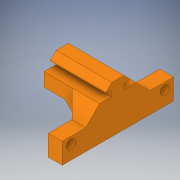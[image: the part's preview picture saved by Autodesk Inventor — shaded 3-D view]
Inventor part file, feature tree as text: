
AUTODESK INVENTOR PART (.ipt)
format: ipt  version: 2019 (Build 230136000, 136)  size: 202,752 bytes
history: native  units: in
note: dims shown in document units (in); Inventor stores cm internally (conversion verified against a paired STEP export)
features: sketch x5, extrude x4, chamfer x3, fillet x1, thicken_offset x1, hole x1, projected_geometry x1
ambient origin geometry x8: Origin, YZ Plane, XZ Plane, XY Plane, X Axis, Y Axis, Z Axis, Center Point
bodies: Body1 (feature_tree)
feature tree (16):
  extrude  "Extrusion2"  Depth=0.1in
  fillet  "Fillet1"  Radius=0.121in
  thicken_offset  "Thicken1"
  extrude  "Extrusion3"  Depth=0.442in
  extrude  "Extrusion4"  TaperAngle=135.0deg  [1 undecoded]
  chamfer  "Chamfer1"  Distance=1.0in
  hole  "Hole1"  [1 undecoded]
  extrude  "Extrusion5"  Depth=0.375in
  chamfer  "Chamfer4"  Distance=0.15in
  chamfer  "Chamfer5"  Distance=0.625in
  sketch  "Sketch1"  dims[d1=0.655in d2=0.1in d9=0.121in]
  sketch  "Sketch2"  dims[d12=0.0in d15=0.442in d16=0.46in]
  sketch  "Sketch3"  dims[d20=135.0deg d21=135.0deg]
  projected_geometry  "Projected Loop1"
  sketch  "Sketch4"  dims[d26=0.115in]
  sketch  "Sketch5"  dims[d38=0.218in d41=1.0in d42=0.0in d43=0.01in d44=0.15in d45=0.15in d46=0.625in d47=0.25in d48=0.0in d49=2.0in d50=0.655in d51=0.6725in d52=0.375in d53=0.25in d54=0.0in d55=0.25in d56=0.125in d57=45.0deg d64=0.154in d66=0.154in d68=0.165in d69=0.75in d70=0.375in d71=0.25in d72=0.5635in d73=1.0in d74=0.8108in d75=0.154in d76=0.154in d77=0.23in d78=0.2125in d79=0.75in d80=0.0in d81=0.244in d82=0.125in d83=45.0deg d84=0.375in d85=0.125in d86=45.0deg]
note: 2 required parameter values undecoded (feature->parameter linkage not recoverable at this tier; creation-order binding heuristic only, values carry confidence <= 0.55)
